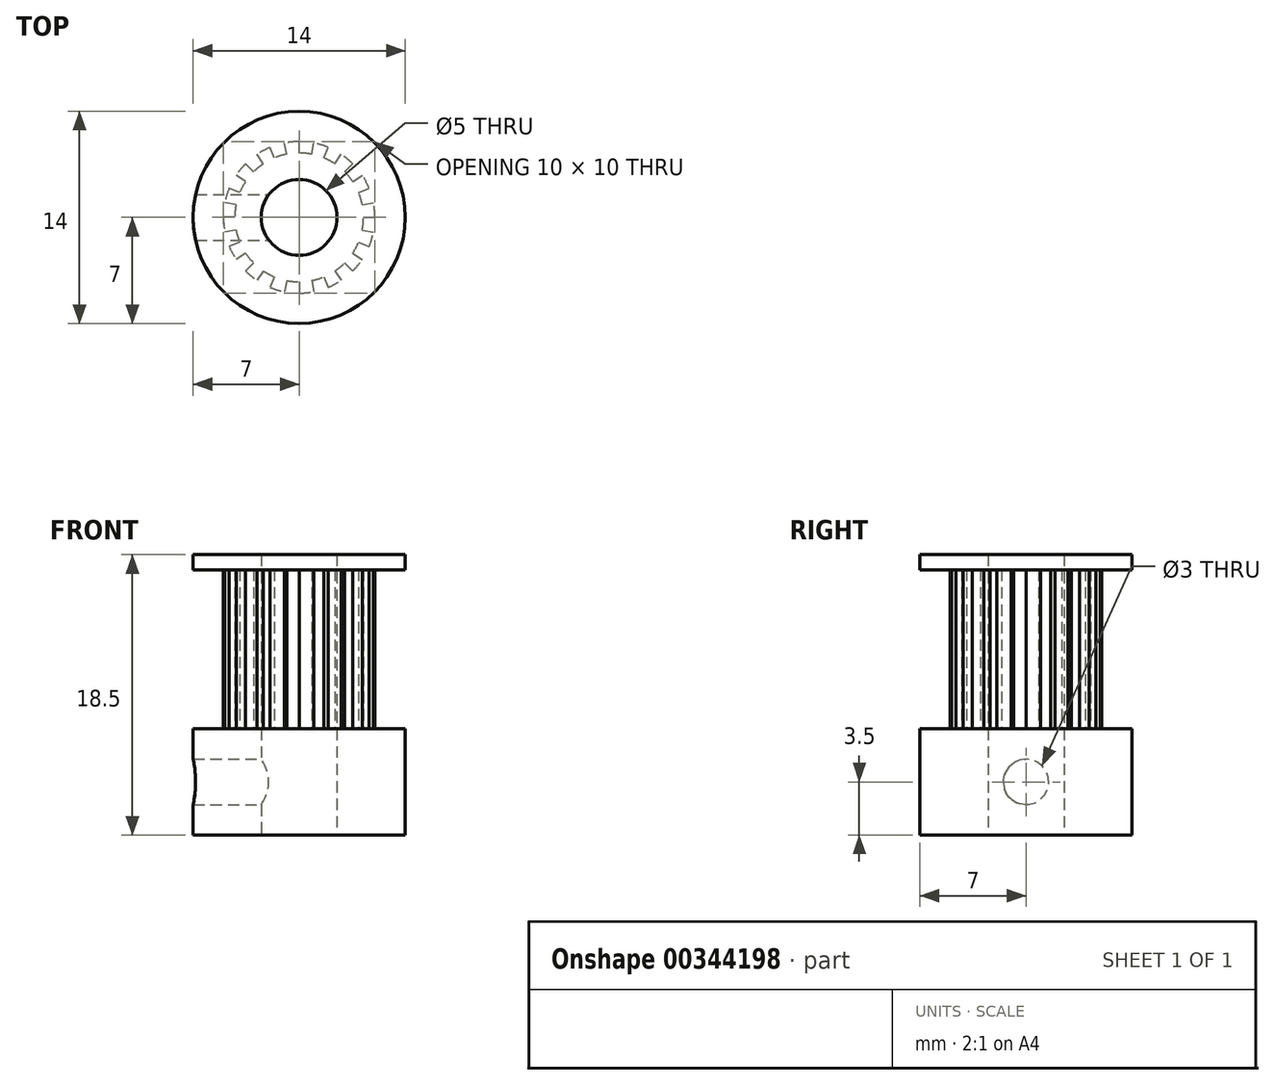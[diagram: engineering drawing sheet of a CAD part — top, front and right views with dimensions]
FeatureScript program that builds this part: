
annotation { "Feature Type Name" : "Feature", "Feature Type Description" : "" }
export const myFeature = defineFeature(function(context is Context, id is Id, definition is map)
    precondition{}
    {
        {
            var Q0;
            Q0=qCreatedBy(makeId("Top.planeOp"),FACE);
            var sketch = newSketch(context, id + "F0", { "sketchPlane" : qUnion([Q0])});
            skCircle(sketch, "E0", {"center": v(0, 0) * mm, "radius": 7 * mm});
            skSolve(sketch);
        }
        {
            var Q0;
            Q0 = qSketchRegion(id + "F0", true);
            extrude(context, id + "F1", {"entities" : qUnion([Q0]), "depth" : 7 * mm});
        }
        {
            var Q0;
            Q0=makeQuery(id+"F1.opExtrude","CAP_FACE",FACE,{"disambiguationData":[OSD([sQuery(id+"F0.wireOp",EDGE,"E0")])],"isStart":false});
            var sketch = newSketch(context, id + "F2", { "sketchPlane" : qUnion([Q0])});
            skLineSegment(sketch, "E1", {"start": v(0, 4.25) * mm, "end": v(0, 5) * mm});
            skLineSegment(sketch, "E2.1.0", {"start": v(-0.83, 4.17) * mm, "end": v(-0.98, 4.9) * mm});
            skLineSegment(sketch, "E2.2.0", {"start": v(-1.63, 3.93) * mm, "end": v(-1.91, 4.62) * mm});
            skLineSegment(sketch, "E2.3.0", {"start": v(-2.36, 3.53) * mm, "end": v(-2.78, 4.16) * mm});
            skLineSegment(sketch, "E2.4.0", {"start": v(-3, 3) * mm, "end": v(-3.54, 3.54) * mm});
            skLineSegment(sketch, "E2.5.0", {"start": v(-3.53, 2.36) * mm, "end": v(-4.16, 2.78) * mm});
            skLineSegment(sketch, "E2.6.0", {"start": v(-3.93, 1.63) * mm, "end": v(-4.62, 1.91) * mm});
            skLineSegment(sketch, "E2.7.0", {"start": v(-4.17, 0.83) * mm, "end": v(-4.9, 0.98) * mm});
            skLineSegment(sketch, "E2.8.0", {"start": v(-4.25, 0) * mm, "end": v(-5, 0) * mm});
            skLineSegment(sketch, "E2.9.0", {"start": v(-4.17, -0.83) * mm, "end": v(-4.9, -0.98) * mm});
            skLineSegment(sketch, "E2.10.0", {"start": v(-3.93, -1.63) * mm, "end": v(-4.62, -1.91) * mm});
            skLineSegment(sketch, "E2.11.0", {"start": v(-3.53, -2.36) * mm, "end": v(-4.16, -2.78) * mm});
            skLineSegment(sketch, "E2.12.0", {"start": v(-3, -3) * mm, "end": v(-3.54, -3.54) * mm});
            skLineSegment(sketch, "E2.13.0", {"start": v(-2.36, -3.53) * mm, "end": v(-2.78, -4.16) * mm});
            skLineSegment(sketch, "E2.14.0", {"start": v(-1.63, -3.93) * mm, "end": v(-1.91, -4.62) * mm});
            skLineSegment(sketch, "E2.15.0", {"start": v(-0.83, -4.17) * mm, "end": v(-0.98, -4.9) * mm});
            skLineSegment(sketch, "E2.16.0", {"start": v(0, -4.25) * mm, "end": v(0, -5) * mm});
            skLineSegment(sketch, "E2.17.0", {"start": v(0.83, -4.17) * mm, "end": v(0.98, -4.9) * mm});
            skLineSegment(sketch, "E2.18.0", {"start": v(1.63, -3.93) * mm, "end": v(1.91, -4.62) * mm});
            skLineSegment(sketch, "E2.19.0", {"start": v(2.36, -3.53) * mm, "end": v(2.78, -4.16) * mm});
            skLineSegment(sketch, "E2.20.0", {"start": v(3, -3) * mm, "end": v(3.54, -3.54) * mm});
            skLineSegment(sketch, "E2.21.0", {"start": v(3.53, -2.36) * mm, "end": v(4.16, -2.78) * mm});
            skLineSegment(sketch, "E2.22.0", {"start": v(3.93, -1.63) * mm, "end": v(4.62, -1.91) * mm});
            skLineSegment(sketch, "E2.23.0", {"start": v(4.17, -0.83) * mm, "end": v(4.9, -0.98) * mm});
            skLineSegment(sketch, "E2.24.0", {"start": v(4.25, 0) * mm, "end": v(5, 0) * mm});
            skLineSegment(sketch, "E2.25.0", {"start": v(4.17, 0.83) * mm, "end": v(4.9, 0.98) * mm});
            skLineSegment(sketch, "E2.26.0", {"start": v(3.93, 1.63) * mm, "end": v(4.62, 1.91) * mm});
            skLineSegment(sketch, "E2.27.0", {"start": v(3.53, 2.36) * mm, "end": v(4.16, 2.78) * mm});
            skLineSegment(sketch, "E2.28.0", {"start": v(3, 3) * mm, "end": v(3.54, 3.54) * mm});
            skLineSegment(sketch, "E2.29.0", {"start": v(2.36, 3.53) * mm, "end": v(2.78, 4.16) * mm});
            skLineSegment(sketch, "E2.30.0", {"start": v(1.63, 3.93) * mm, "end": v(1.91, 4.62) * mm});
            skLineSegment(sketch, "E2.31.0", {"start": v(0.83, 4.17) * mm, "end": v(0.98, 4.9) * mm});
            skPoint(sketch, "E2.center", {"position": v(0, 0) * mm});
            skArc(sketch, "E3", {"start": v(-0.83, 4.17) * mm, "mid": v(-1.23, 4.07) * mm, "end": v(-1.63, 3.93) * mm});
            skArc(sketch, "E4", {"start": v(-1.91, 4.62) * mm, "mid": v(-2.36, 4.4) * mm, "end": v(-2.78, 4.16) * mm});
            skPoint(sketch, "E5.orphan", {"position": v(-1.14, 5.75) * mm});
            skArc(sketch, "E6.trimOffspring", {"start": v(0, 5) * mm, "mid": v(-0.5, 4.98) * mm, "end": v(-0.98, 4.9) * mm});
            skArc(sketch, "E7.trimOffspring", {"start": v(0.83, 4.17) * mm, "mid": v(0.42, 4.23) * mm, "end": v(0, 4.25) * mm});
            skArc(sketch, "E8.trimOffspring", {"start": v(1.91, 4.62) * mm, "mid": v(1.45, 4.78) * mm, "end": v(0.98, 4.9) * mm});
            skArc(sketch, "E9.trimOffspring", {"start": v(2.36, 3.53) * mm, "mid": v(2, 3.75) * mm, "end": v(1.63, 3.93) * mm});
            skArc(sketch, "E10.trimOffspring", {"start": v(3.54, 3.54) * mm, "mid": v(3.17, 3.87) * mm, "end": v(2.78, 4.16) * mm});
            skArc(sketch, "E11.trimOffspring", {"start": v(3.53, 2.36) * mm, "mid": v(3.29, 2.7) * mm, "end": v(3, 3) * mm});
            skArc(sketch, "E12.trimOffspring", {"start": v(4.62, 1.91) * mm, "mid": v(4.4, 2.36) * mm, "end": v(4.16, 2.78) * mm});
            skArc(sketch, "E13.trimOffspring", {"start": v(4.17, 0.83) * mm, "mid": v(4.07, 1.23) * mm, "end": v(3.93, 1.63) * mm});
            skArc(sketch, "E14.trimOffspring", {"start": v(5, 0) * mm, "mid": v(4.98, 0.5) * mm, "end": v(4.9, 0.98) * mm});
            skArc(sketch, "E15.trimOffspring", {"start": v(4.17, -0.83) * mm, "mid": v(4.23, -0.42) * mm, "end": v(4.25, 0) * mm});
            skArc(sketch, "E16.trimOffspring", {"start": v(4.62, -1.91) * mm, "mid": v(4.78, -1.45) * mm, "end": v(4.9, -0.98) * mm});
            skArc(sketch, "E17.trimOffspring", {"start": v(3.53, -2.36) * mm, "mid": v(3.75, -2) * mm, "end": v(3.93, -1.63) * mm});
            skArc(sketch, "E18.trimOffspring", {"start": v(3.54, -3.54) * mm, "mid": v(3.87, -3.17) * mm, "end": v(4.16, -2.78) * mm});
            skArc(sketch, "E19.trimOffspring", {"start": v(2.36, -3.53) * mm, "mid": v(2.7, -3.29) * mm, "end": v(3, -3) * mm});
            skArc(sketch, "E20.trimOffspring", {"start": v(1.91, -4.62) * mm, "mid": v(2.36, -4.4) * mm, "end": v(2.78, -4.16) * mm});
            skArc(sketch, "E21.trimOffspring", {"start": v(0.83, -4.17) * mm, "mid": v(1.23, -4.07) * mm, "end": v(1.63, -3.93) * mm});
            skArc(sketch, "E22.trimOffspring", {"start": v(0, -5) * mm, "mid": v(0.5, -4.98) * mm, "end": v(0.98, -4.9) * mm});
            skArc(sketch, "E23.trimOffspring", {"start": v(-0.83, -4.17) * mm, "mid": v(-0.42, -4.23) * mm, "end": v(0, -4.25) * mm});
            skArc(sketch, "E24.trimOffspring", {"start": v(-2.36, -3.53) * mm, "mid": v(-2, -3.75) * mm, "end": v(-1.63, -3.93) * mm});
            skArc(sketch, "E25.trimOffspring", {"start": v(-3.53, -2.36) * mm, "mid": v(-3.29, -2.7) * mm, "end": v(-3, -3) * mm});
            skArc(sketch, "E26.trimOffspring", {"start": v(-4.17, -0.83) * mm, "mid": v(-4.07, -1.23) * mm, "end": v(-3.93, -1.63) * mm});
            skArc(sketch, "E27.trimOffspring", {"start": v(-4.17, 0.83) * mm, "mid": v(-4.23, 0.42) * mm, "end": v(-4.25, 0) * mm});
            skArc(sketch, "E28.trimOffspring", {"start": v(-3.53, 2.36) * mm, "mid": v(-3.75, 2) * mm, "end": v(-3.93, 1.63) * mm});
            skArc(sketch, "E29.trimOffspring", {"start": v(-2.36, 3.53) * mm, "mid": v(-2.7, 3.29) * mm, "end": v(-3, 3) * mm});
            skArc(sketch, "E30.trimOffspring", {"start": v(-3.54, 3.54) * mm, "mid": v(-3.87, 3.17) * mm, "end": v(-4.16, 2.78) * mm});
            skArc(sketch, "E31.trimOffspring", {"start": v(-4.62, 1.91) * mm, "mid": v(-4.78, 1.45) * mm, "end": v(-4.9, 0.98) * mm});
            skArc(sketch, "E32.trimOffspring", {"start": v(-5, 0) * mm, "mid": v(-4.98, -0.5) * mm, "end": v(-4.9, -0.98) * mm});
            skArc(sketch, "E33.trimOffspring", {"start": v(-4.62, -1.91) * mm, "mid": v(-4.4, -2.36) * mm, "end": v(-4.16, -2.78) * mm});
            skArc(sketch, "E34.trimOffspring", {"start": v(-3.54, -3.54) * mm, "mid": v(-3.17, -3.87) * mm, "end": v(-2.78, -4.16) * mm});
            skArc(sketch, "E35.trimOffspring", {"start": v(-1.91, -4.62) * mm, "mid": v(-1.45, -4.78) * mm, "end": v(-0.98, -4.9) * mm});
            skPoint(sketch, "E36.orphan", {"position": v(1.14, 5.75) * mm});
            skPoint(sketch, "E37.orphan", {"position": v(0, 5.86) * mm});
            skPoint(sketch, "E38.orphan", {"position": v(2.24, 5.41) * mm});
            skPoint(sketch, "E39.orphan", {"position": v(3.25, 4.87) * mm});
            skPoint(sketch, "E40.orphan", {"position": v(4.14, 4.14) * mm});
            skPoint(sketch, "E41.orphan", {"position": v(4.87, 3.25) * mm});
            skPoint(sketch, "E42.orphan", {"position": v(5.41, 2.24) * mm});
            skPoint(sketch, "E43.orphan", {"position": v(5.75, 1.14) * mm});
            skPoint(sketch, "E44.orphan", {"position": v(5.86, 0) * mm});
            skPoint(sketch, "E45.orphan", {"position": v(5.75, -1.14) * mm});
            skPoint(sketch, "E46.orphan", {"position": v(5.41, -2.24) * mm});
            skPoint(sketch, "E47.orphan", {"position": v(4.87, -3.25) * mm});
            skPoint(sketch, "E48.orphan", {"position": v(4.14, -4.14) * mm});
            skPoint(sketch, "E49.orphan", {"position": v(3.25, -4.87) * mm});
            skPoint(sketch, "E50.orphan", {"position": v(2.24, -5.41) * mm});
            skPoint(sketch, "E51.orphan", {"position": v(1.14, -5.75) * mm});
            skPoint(sketch, "E52.orphan", {"position": v(0, -5.86) * mm});
            skPoint(sketch, "E53.orphan", {"position": v(-1.14, -5.75) * mm});
            skPoint(sketch, "E54.orphan", {"position": v(-2.24, -5.41) * mm});
            skPoint(sketch, "E55.orphan", {"position": v(-3.25, -4.87) * mm});
            skPoint(sketch, "E56.orphan", {"position": v(-4.14, -4.14) * mm});
            skPoint(sketch, "E57.orphan", {"position": v(-4.87, -3.25) * mm});
            skPoint(sketch, "E58.orphan", {"position": v(-5.41, -2.24) * mm});
            skPoint(sketch, "E59.orphan", {"position": v(-5.75, -1.14) * mm});
            skPoint(sketch, "E60.orphan", {"position": v(-5.86, 0) * mm});
            skPoint(sketch, "E61.orphan", {"position": v(-5.75, 1.14) * mm});
            skPoint(sketch, "E62.orphan", {"position": v(-5.41, 2.24) * mm});
            skPoint(sketch, "E63.orphan", {"position": v(-4.87, 3.25) * mm});
            skPoint(sketch, "E64.orphan", {"position": v(-4.14, 4.14) * mm});
            skPoint(sketch, "E65.orphan", {"position": v(-3.25, 4.87) * mm});
            skPoint(sketch, "E66.orphan", {"position": v(-2.24, 5.41) * mm});
            skSolve(sketch);
        }
        {
            var Q0;
            Q0 = qSketchRegion(id + "F2", true);
            extrude(context, id + "F3", {"entities" : qUnion([Q0]), "operationType" : NewBodyOperationType.ADD, "depth" : 10.5 * mm});
        }
        {
            var Q0;
            Q0=makeQuery(id+"F3.opExtrude","CAP_FACE",FACE,{"disambiguationData":[OSD([sQuery(id+"F2.wireOp",EDGE,"E1"),sQuery(id+"F2.wireOp",EDGE,"E2.1.0"),sQuery(id+"F2.wireOp",EDGE,"E2.2.0"),sQuery(id+"F2.wireOp",EDGE,"E2.3.0"),sQuery(id+"F2.wireOp",EDGE,"E2.4.0"),sQuery(id+"F2.wireOp",EDGE,"E2.5.0"),sQuery(id+"F2.wireOp",EDGE,"E2.6.0"),sQuery(id+"F2.wireOp",EDGE,"E2.7.0"),sQuery(id+"F2.wireOp",EDGE,"E2.8.0"),sQuery(id+"F2.wireOp",EDGE,"E2.9.0"),sQuery(id+"F2.wireOp",EDGE,"E2.10.0"),sQuery(id+"F2.wireOp",EDGE,"E2.11.0"),sQuery(id+"F2.wireOp",EDGE,"E2.12.0"),sQuery(id+"F2.wireOp",EDGE,"E2.13.0"),sQuery(id+"F2.wireOp",EDGE,"E2.14.0"),sQuery(id+"F2.wireOp",EDGE,"E2.15.0"),sQuery(id+"F2.wireOp",EDGE,"E2.16.0"),sQuery(id+"F2.wireOp",EDGE,"E2.17.0"),sQuery(id+"F2.wireOp",EDGE,"E2.18.0"),sQuery(id+"F2.wireOp",EDGE,"E2.19.0"),sQuery(id+"F2.wireOp",EDGE,"E2.20.0"),sQuery(id+"F2.wireOp",EDGE,"E2.21.0"),sQuery(id+"F2.wireOp",EDGE,"E2.22.0"),sQuery(id+"F2.wireOp",EDGE,"E2.23.0"),sQuery(id+"F2.wireOp",EDGE,"E2.24.0"),sQuery(id+"F2.wireOp",EDGE,"E2.25.0"),sQuery(id+"F2.wireOp",EDGE,"E2.26.0"),sQuery(id+"F2.wireOp",EDGE,"E2.27.0"),sQuery(id+"F2.wireOp",EDGE,"E2.28.0"),sQuery(id+"F2.wireOp",EDGE,"E2.29.0"),sQuery(id+"F2.wireOp",EDGE,"E2.30.0"),sQuery(id+"F2.wireOp",EDGE,"E2.31.0"),sQuery(id+"F2.wireOp",EDGE,"E3"),sQuery(id+"F2.wireOp",EDGE,"E4"),sQuery(id+"F2.wireOp",EDGE,"E6.trimOffspring"),sQuery(id+"F2.wireOp",EDGE,"E7.trimOffspring"),sQuery(id+"F2.wireOp",EDGE,"E8.trimOffspring"),sQuery(id+"F2.wireOp",EDGE,"E9.trimOffspring"),sQuery(id+"F2.wireOp",EDGE,"E10.trimOffspring"),sQuery(id+"F2.wireOp",EDGE,"E11.trimOffspring"),sQuery(id+"F2.wireOp",EDGE,"E12.trimOffspring"),sQuery(id+"F2.wireOp",EDGE,"E13.trimOffspring"),sQuery(id+"F2.wireOp",EDGE,"E14.trimOffspring"),sQuery(id+"F2.wireOp",EDGE,"E15.trimOffspring"),sQuery(id+"F2.wireOp",EDGE,"E16.trimOffspring"),sQuery(id+"F2.wireOp",EDGE,"E17.trimOffspring"),sQuery(id+"F2.wireOp",EDGE,"E18.trimOffspring"),sQuery(id+"F2.wireOp",EDGE,"E19.trimOffspring"),sQuery(id+"F2.wireOp",EDGE,"E20.trimOffspring"),sQuery(id+"F2.wireOp",EDGE,"E21.trimOffspring"),sQuery(id+"F2.wireOp",EDGE,"E22.trimOffspring"),sQuery(id+"F2.wireOp",EDGE,"E23.trimOffspring"),sQuery(id+"F2.wireOp",EDGE,"E24.trimOffspring"),sQuery(id+"F2.wireOp",EDGE,"E25.trimOffspring"),sQuery(id+"F2.wireOp",EDGE,"E26.trimOffspring"),sQuery(id+"F2.wireOp",EDGE,"E27.trimOffspring"),sQuery(id+"F2.wireOp",EDGE,"E28.trimOffspring"),sQuery(id+"F2.wireOp",EDGE,"E29.trimOffspring"),sQuery(id+"F2.wireOp",EDGE,"E30.trimOffspring"),sQuery(id+"F2.wireOp",EDGE,"E31.trimOffspring"),sQuery(id+"F2.wireOp",EDGE,"E32.trimOffspring"),sQuery(id+"F2.wireOp",EDGE,"E33.trimOffspring"),sQuery(id+"F2.wireOp",EDGE,"E34.trimOffspring"),sQuery(id+"F2.wireOp",EDGE,"E35.trimOffspring")])],"isStart":false});
            var sketch = newSketch(context, id + "F4", { "sketchPlane" : qUnion([Q0])});
            skCircle(sketch, "E67", {"center": v(0, 0) * mm, "radius": 7 * mm});
            skLineSegment(sketch, "E68", {"start": v(0, -4.25) * mm, "end": v(0, 4.25) * mm, "construction": true});
            skLineSegment(sketch, "E69", {"start": v(4.25, 0) * mm, "end": v(-4.25, 0) * mm, "construction": true});
            skSolve(sketch);
        }
        {
            var Q0;
            Q0 = qSketchRegion(id + "F4", true);
            extrude(context, id + "F5", {"entities" : qUnion([Q0]), "operationType" : NewBodyOperationType.ADD, "depth" : 1 * mm});
        }
        {
            var Q0;
            Q0=makeQuery(id+"F1.opExtrude","CAP_FACE",FACE,{"disambiguationData":[OSD([sQuery(id+"F0.wireOp",EDGE,"E0")])],"isStart":true});
            var sketch = newSketch(context, id + "F6", { "sketchPlane" : qUnion([Q0])});
            skCircle(sketch, "E70", {"center": v(0, 0) * mm, "radius": 2.5 * mm});
            skSolve(sketch);
        }
        {
            var Q0;
            Q0 = qSketchRegion(id + "F6", true);
            extrude(context, id + "F7", {"entities" : qUnion([Q0]), "operationType" : NewBodyOperationType.REMOVE, "endBound" : BoundingType.THROUGH_ALL, "oppositeDirection" : true, "depth" : 25 * mm});
        }
        {
            var Q0;
            Q0=qCreatedBy(makeId("Right.planeOp"),FACE);
            var sketch = newSketch(context, id + "F8", { "sketchPlane" : qUnion([Q0])});
            skCircle(sketch, "E71", {"center": v(0, 3.5) * mm, "radius": 1.5 * mm});
            skSolve(sketch);
        }
        {
            var Q0;
            Q0 = qSketchRegion(id + "F8", true);
            extrude(context, id + "F9", {"entities" : qUnion([Q0]), "operationType" : NewBodyOperationType.REMOVE, "oppositeDirection" : true, "depth" : 25 * mm});
        }
    });
